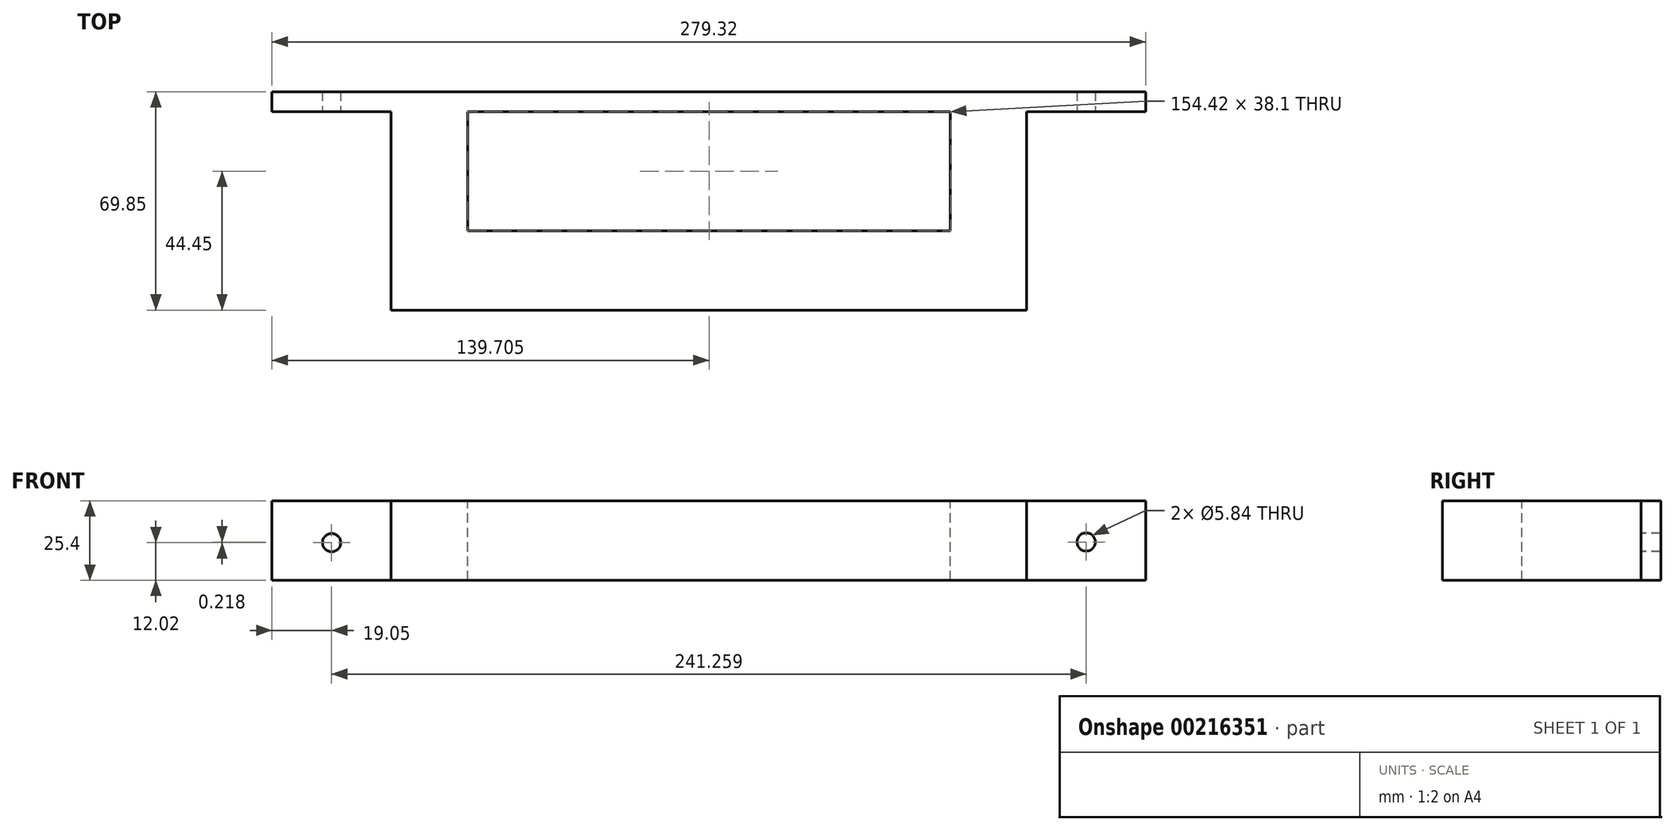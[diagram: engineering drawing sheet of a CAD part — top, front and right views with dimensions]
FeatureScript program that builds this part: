
annotation { "Feature Type Name" : "Feature", "Feature Type Description" : "" }
export const myFeature = defineFeature(function(context is Context, id is Id, definition is map)
    precondition{}
    {
        {
            var Q0;
            Q0=qCreatedBy(makeId("Top.planeOp"),FACE);
            var sketch = newSketch(context, id + "F0", { "sketchPlane" : qUnion([Q0])});
            skLineSegment(sketch, "E0.bottom", {"start": v(101.6, 12.7) * mm, "end": v(-101.6, 12.7) * mm});
            skLineSegment(sketch, "E0.top", {"start": v(101.6, -12.7) * mm, "end": v(-101.6, -12.7) * mm});
            skLineSegment(sketch, "E0.left", {"start": v(101.6, 12.7) * mm, "end": v(101.6, -12.7) * mm});
            skLineSegment(sketch, "E0.right", {"start": v(-101.6, 12.7) * mm, "end": v(-101.6, -12.7) * mm});
            skPoint(sketch, "E0.middle", {"position": v(0, 0) * mm});
            skSolve(sketch);
        }
        {
            var Q0;
            Q0 = qSketchRegion(id + "F0", true);
            extrude(context, id + "F1", {"entities" : qUnion([Q0]), "depth" : 25.4 * mm});
        }
        {
            var Q0;
            Q0=makeQuery(id+"F1.opExtrude","SWEPT_FACE",FACE,{"disambiguationData":[OSD([sQuery(id+"F0.wireOp",EDGE,"E0.bottom")])]});
            var sketch = newSketch(context, id + "F2", { "sketchPlane" : qUnion([Q0])});
            skLineSegment(sketch, "E1.bottom", {"start": v(101.6, 0) * mm, "end": v(77.2, 0) * mm});
            skLineSegment(sketch, "E1.top", {"start": v(101.6, 25.4) * mm, "end": v(77.2, 25.4) * mm});
            skLineSegment(sketch, "E1.left", {"start": v(101.6, 0) * mm, "end": v(101.6, 25.4) * mm});
            skLineSegment(sketch, "E1.right", {"start": v(77.2, 0) * mm, "end": v(77.2, 25.4) * mm});
            skLineSegment(sketch, "E2.bottom", {"start": v(-101.6, 0) * mm, "end": v(-77.22, 0) * mm});
            skLineSegment(sketch, "E2.top", {"start": v(-101.6, 25.4) * mm, "end": v(-77.22, 25.4) * mm});
            skLineSegment(sketch, "E2.left", {"start": v(-101.6, 0) * mm, "end": v(-101.6, 25.4) * mm});
            skLineSegment(sketch, "E2.right", {"start": v(-77.22, 0) * mm, "end": v(-77.22, 25.4) * mm});
            skSolve(sketch);
        }
        {
            var Q0;
            Q0 = qSketchRegion(id + "F2", true);
            extrude(context, id + "F3", {"entities" : qUnion([Q0]), "operationType" : NewBodyOperationType.ADD, "depth" : 38.1 * mm});
        }
        {
            var Q0;
            Q0=makeQuery(id+"F3.opExtrude","CAP_FACE",FACE,{"disambiguationData":[OSD([sQuery(id+"F2.wireOp",EDGE,"E1.bottom"),sQuery(id+"F2.wireOp",EDGE,"E1.top"),sQuery(id+"F2.wireOp",EDGE,"E1.left"),sQuery(id+"F2.wireOp",EDGE,"E1.right")])],"isStart":false});
            var sketch = newSketch(context, id + "F4", { "sketchPlane" : qUnion([Q0])});
            skLineSegment(sketch, "E3.bottom", {"start": v(101.6, 0) * mm, "end": v(139.7, 0) * mm});
            skLineSegment(sketch, "E3.top", {"start": v(101.6, 25.4) * mm, "end": v(139.7, 25.4) * mm});
            skLineSegment(sketch, "E3.left", {"start": v(101.6, 0) * mm, "end": v(101.6, 25.4) * mm});
            skLineSegment(sketch, "E3.right", {"start": v(139.7, 0) * mm, "end": v(139.7, 25.4) * mm});
            skLineSegment(sketch, "E4.bottom", {"start": v(101.6, 0) * mm, "end": v(-101.52, 0) * mm});
            skLineSegment(sketch, "E4.top", {"start": v(101.6, 25.4) * mm, "end": v(-101.52, 25.4) * mm});
            skLineSegment(sketch, "E4.right", {"start": v(-101.52, 0) * mm, "end": v(-101.52, 25.4) * mm});
            skLineSegment(sketch, "E5.bottom", {"start": v(-101.52, 0) * mm, "end": v(-139.62, 0) * mm});
            skLineSegment(sketch, "E5.top", {"start": v(-101.52, 25.4) * mm, "end": v(-139.62, 25.4) * mm});
            skLineSegment(sketch, "E5.right", {"start": v(-139.62, 0) * mm, "end": v(-139.62, 25.4) * mm});
            skSolve(sketch);
        }
        {
            var Q0;
            Q0 = qSketchRegion(id + "F4", true);
            extrude(context, id + "F5", {"entities" : qUnion([Q0]), "operationType" : NewBodyOperationType.ADD, "depth" : 6.35 * mm});
        }
        {
            var Q0;
            {var subQ0=sQuery(id+"F4.wireOp",EDGE,"E5.top");var subQ1=sQuery(id+"F4.wireOp",EDGE,"E4.top");var subQ2=sQuery(id+"F4.wireOp",EDGE,"E3.top");var subQ3=sQuery(id+"F4.wireOp",EDGE,"E5.bottom");var subQ4=sQuery(id+"F4.wireOp",EDGE,"E4.bottom");var subQ5=sQuery(id+"F4.wireOp",EDGE,"E3.bottom");var subQ6=sQuery(id+"F0.wireOp",EDGE,"E0.right");var subQ10=sQuery(id+"F4.wireOp",EDGE,"E3.right");Q0=makeQuery(id+"F5.boolean.opBoolean","SPLIT",FACE,{"disambiguationData":[TD([makeQuery(id+"F1.opExtrude","SWEPT_FACE",FACE,{"disambiguationData":[OSD([subQ6])]})])],"derivedFrom":makeQuery(id+"F5.opExtrude","CAP_FACE",FACE,{"disambiguationData":[OSD([subQ5,subQ2,subQ10,subQ4,subQ1,subQ3,subQ0,sQuery(id+"F4.wireOp",EDGE,"E5.right")])],"isStart":true})});}
            var sketch = newSketch(context, id + "F6", { "sketchPlane" : qUnion([Q0])});
            skCircle(sketch, "E6", {"center": v(-120.65, 12.02) * mm, "radius": 2.92 * mm});
            skPoint(sketch, "E6.centerSnap0", {"position": v(-120.65, 25.4) * mm});
            skSolve(sketch);
        }
        {
            var Q0;
            Q0 = qSketchRegion(id + "F6", true);
            extrude(context, id + "F7", {"entities" : qUnion([Q0]), "operationType" : NewBodyOperationType.REMOVE, "oppositeDirection" : true, "depth" : 25.4 * mm});
        }
        {
            var Q0;
            {var subQ0=sQuery(id+"F4.wireOp",EDGE,"E5.top");var subQ1=sQuery(id+"F4.wireOp",EDGE,"E4.top");var subQ2=sQuery(id+"F4.wireOp",EDGE,"E3.top");var subQ3=sQuery(id+"F4.wireOp",EDGE,"E5.bottom");var subQ4=sQuery(id+"F4.wireOp",EDGE,"E4.bottom");var subQ5=sQuery(id+"F4.wireOp",EDGE,"E3.bottom");var subQ7=sQuery(id+"F0.wireOp",EDGE,"E0.left");var subQ10=sQuery(id+"F4.wireOp",EDGE,"E5.right");Q0=makeQuery(id+"F5.boolean.opBoolean","SPLIT",FACE,{"disambiguationData":[TD([makeQuery(id+"F1.opExtrude","SWEPT_FACE",FACE,{"disambiguationData":[OSD([subQ7])]})])],"derivedFrom":makeQuery(id+"F5.opExtrude","CAP_FACE",FACE,{"disambiguationData":[OSD([subQ5,subQ2,sQuery(id+"F4.wireOp",EDGE,"E3.right"),subQ4,subQ1,subQ3,subQ0,subQ10])],"isStart":true})});}
            var sketch = newSketch(context, id + "F8", { "sketchPlane" : qUnion([Q0])});
            skCircle(sketch, "E7", {"center": v(120.6, 12.24) * mm, "radius": 2.92 * mm});
            skPoint(sketch, "E7.centerSnap0", {"position": v(120.6, 25.4) * mm});
            skSolve(sketch);
        }
        {
            var Q0;
            Q0 = qSketchRegion(id + "F8", true);
            extrude(context, id + "F9", {"entities" : qUnion([Q0]), "operationType" : NewBodyOperationType.REMOVE, "oppositeDirection" : true, "depth" : 25.4 * mm});
        }
    });
